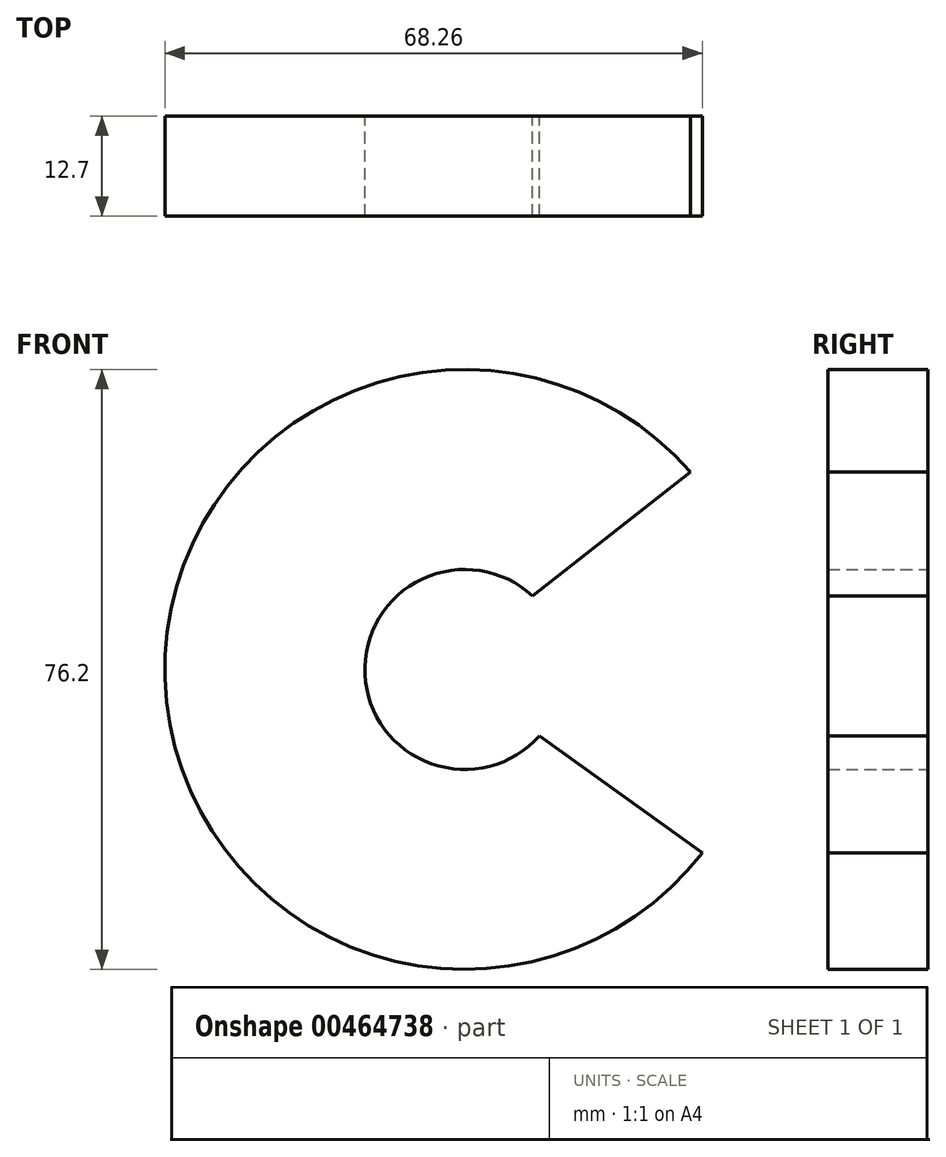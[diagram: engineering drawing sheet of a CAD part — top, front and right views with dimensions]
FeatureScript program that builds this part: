
annotation { "Feature Type Name" : "Feature", "Feature Type Description" : "" }
export const myFeature = defineFeature(function(context is Context, id is Id, definition is map)
    precondition{}
    {
        {
            var Q0;
            Q0=qCreatedBy(makeId("Front.planeOp"),FACE);
            var sketch = newSketch(context, id + "F0", { "sketchPlane" : qUnion([Q0])});
            skArc(sketch, "E0", {"start": v(28.7, 25.06) * mm, "mid": v(-38.08, -1.15) * mm, "end": v(30.16, -23.28) * mm});
            skArc(sketch, "E1", {"start": v(8.6, 9.35) * mm, "mid": v(-12.68, -0.63) * mm, "end": v(9.47, -8.46) * mm});
            skLineSegment(sketch, "E2", {"start": v(8.6, 9.35) * mm, "end": v(28.7, 25.06) * mm});
            skLineSegment(sketch, "E3", {"start": v(9.47, -8.46) * mm, "end": v(30.16, -23.28) * mm});
            skSolve(sketch);
        }
        {
            var Q0;
            Q0 = qSketchRegion(id + "F0", true);
            extrude(context, id + "F1", {"entities" : qUnion([Q0]), "depth" : 12.7 * mm});
        }
    });
